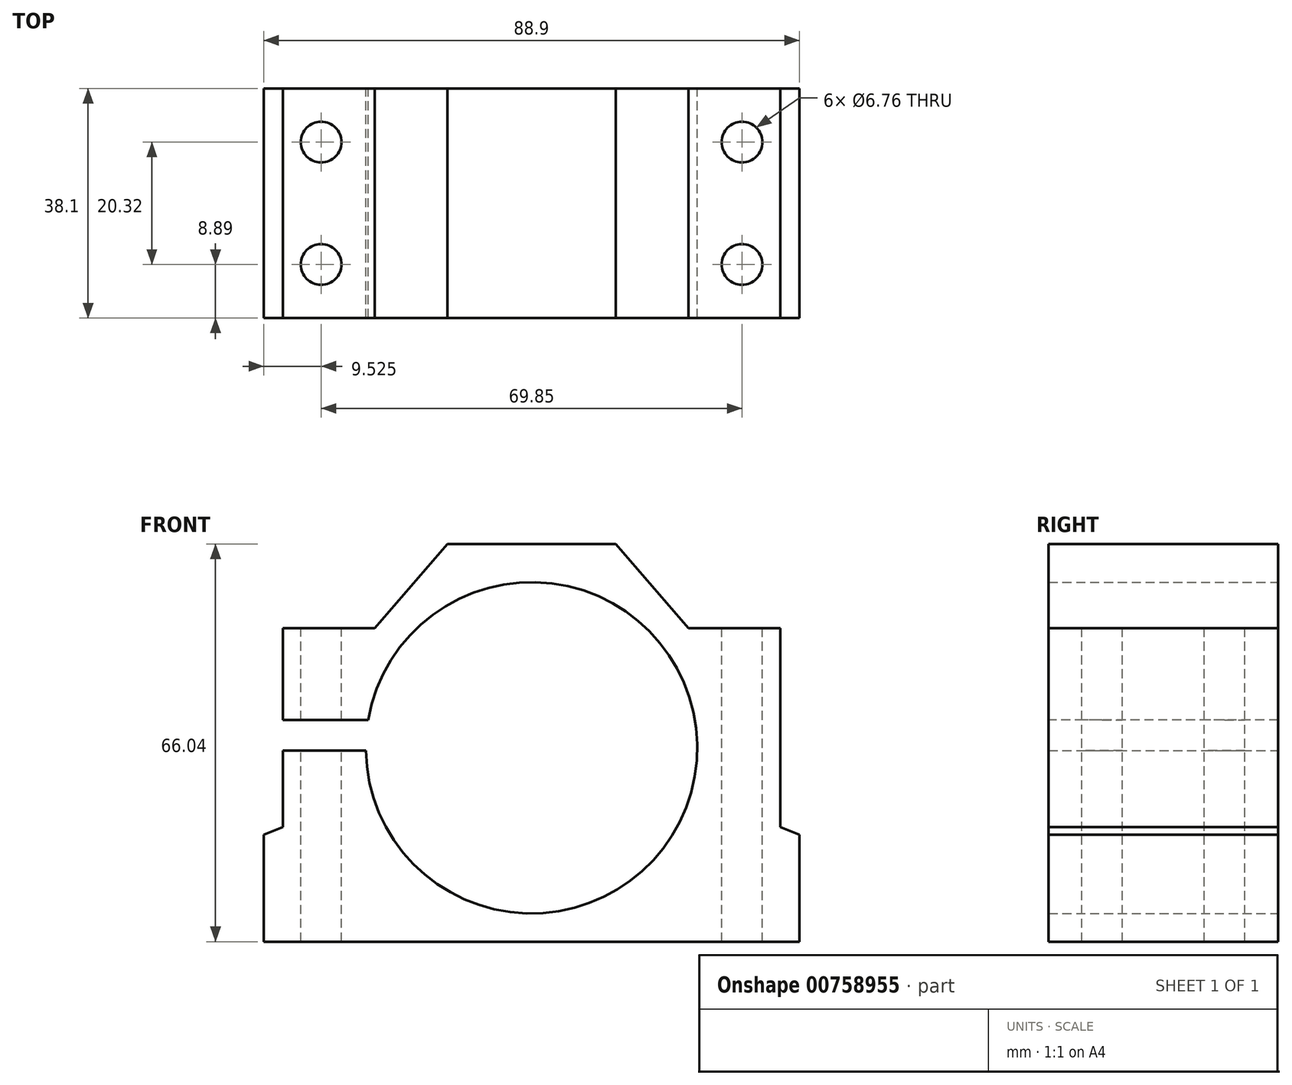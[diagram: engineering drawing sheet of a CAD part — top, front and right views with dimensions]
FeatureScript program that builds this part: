
annotation { "Feature Type Name" : "Feature", "Feature Type Description" : "" }
export const myFeature = defineFeature(function(context is Context, id is Id, definition is map)
    precondition{}
    {
        {
            var Q0;
            Q0=qCreatedBy(makeId("Front.planeOp"),FACE);
            var sketch = newSketch(context, id + "F0", { "sketchPlane" : qUnion([Q0])});
            skLineSegment(sketch, "E0", {"start": v(0, 0) * mm, "end": v(44.45, 0) * mm});
            skLineSegment(sketch, "E1", {"start": v(44.45, 0) * mm, "end": v(44.45, 17.78) * mm});
            skLineSegment(sketch, "E2", {"start": v(44.45, 17.78) * mm, "end": v(41.28, 19.05) * mm});
            skLineSegment(sketch, "E3", {"start": v(41.28, 19.05) * mm, "end": v(41.28, 52.07) * mm});
            skLineSegment(sketch, "E4", {"start": v(41.28, 52.07) * mm, "end": v(26.04, 52.07) * mm});
            skLineSegment(sketch, "E5", {"start": v(26.04, 52.07) * mm, "end": v(13.97, 66.04) * mm});
            skLineSegment(sketch, "E6", {"start": v(13.97, 66.04) * mm, "end": v(0, 66.04) * mm});
            skLineSegment(sketch, "E7.MirrorCS", {"start": v(-41.28, 19.05) * mm, "end": v(-41.28, 52.07) * mm});
            skLineSegment(sketch, "E8.MirrorCS", {"start": v(-44.45, 17.78) * mm, "end": v(-41.28, 19.05) * mm});
            skLineSegment(sketch, "E9.MirrorCS", {"start": v(-41.28, 52.07) * mm, "end": v(-26.04, 52.07) * mm});
            skLineSegment(sketch, "E10.MirrorCS", {"start": v(0, 0) * mm, "end": v(-44.45, 0) * mm});
            skLineSegment(sketch, "E11.MirrorCS", {"start": v(-13.97, 66.04) * mm, "end": v(0, 66.04) * mm});
            skLineSegment(sketch, "E12.MirrorCS", {"start": v(-26.04, 52.07) * mm, "end": v(-13.97, 66.04) * mm});
            skLineSegment(sketch, "E13.MirrorCS", {"start": v(-44.45, 0) * mm, "end": v(-44.45, 17.78) * mm});
            skCircle(sketch, "E14", {"center": v(0, 32.2) * mm, "radius": 27.5 * mm});
            skSolve(sketch);
        }
        {
            var Q0;
            Q0=qSketchRegion(id+"F0",true);
            extrude(context, id + "F1", {"entities" : qUnion([Q0]), "depth" : 38.1 * mm, "offsetDistance" : 25.4 * mm});
        }
        {
            var Q0;
            Q0=makeQuery(id+"F1.opExtrude","CAP_FACE",FACE,{"disambiguationData":[OSD([sQuery(id+"F0.wireOp",EDGE,"E0"),sQuery(id+"F0.wireOp",EDGE,"E1"),sQuery(id+"F0.wireOp",EDGE,"E2"),sQuery(id+"F0.wireOp",EDGE,"E3"),sQuery(id+"F0.wireOp",EDGE,"E4"),sQuery(id+"F0.wireOp",EDGE,"E5"),sQuery(id+"F0.wireOp",EDGE,"E6"),sQuery(id+"F0.wireOp",EDGE,"E7.MirrorCS"),sQuery(id+"F0.wireOp",EDGE,"E8.MirrorCS"),sQuery(id+"F0.wireOp",EDGE,"E9.MirrorCS"),sQuery(id+"F0.wireOp",EDGE,"E10.MirrorCS"),sQuery(id+"F0.wireOp",EDGE,"E11.MirrorCS"),sQuery(id+"F0.wireOp",EDGE,"E12.MirrorCS"),sQuery(id+"F0.wireOp",EDGE,"E13.MirrorCS"),sQuery(id+"F0.wireOp",EDGE,"E14")])],"isStart":false});
            var sketch = newSketch(context, id + "F2", { "sketchPlane" : qUnion([Q0])});
            skLineSegment(sketch, "E15.bottom", {"start": v(-41.28, 31.75) * mm, "end": v(-22.23, 31.75) * mm});
            skLineSegment(sketch, "E15.top", {"start": v(-41.28, 36.83) * mm, "end": v(-22.23, 36.83) * mm});
            skLineSegment(sketch, "E15.left", {"start": v(-41.28, 31.75) * mm, "end": v(-41.28, 36.83) * mm});
            skLineSegment(sketch, "E15.right", {"start": v(-22.23, 31.75) * mm, "end": v(-22.23, 36.83) * mm});
            skSolve(sketch);
        }
        {
            var Q0;
            Q0=qSketchRegion(id+"F2",true);
            extrude(context, id + "F3", {"entities" : qUnion([Q0]), "operationType" : NewBodyOperationType.REMOVE, "endBound" : BoundingType.UP_TO_NEXT, "oppositeDirection" : true, "depth" : 25.4 * mm, "offsetDistance" : 25.4 * mm});
        }
        {
            var Q0;
            Q0=makeQuery(id+"F1.opExtrude","SWEPT_FACE",FACE,{"disambiguationData":[OSD([sQuery(id+"F0.wireOp",EDGE,"E9.MirrorCS")])]});
            var sketch = newSketch(context, id + "F4", { "sketchPlane" : qUnion([Q0])});
            skLineSegment(sketch, "E16", {"start": v(-41.28, -19.05) * mm, "end": v(41.4, -19.05) * mm, "construction": true});
            skPoint(sketch, "E17", {"position": v(-34.93, -29.21) * mm});
            skPoint(sketch, "E18.MirrorP", {"position": v(-34.93, -8.89) * mm});
            skPoint(sketch, "E19.MirrorP", {"position": v(34.93, -8.89) * mm});
            skPoint(sketch, "E20.MirrorP", {"position": v(34.93, -29.21) * mm});
            skSolve(sketch);
        }
        {
            var Q0;
            Q0=sQuery(id+"F4.wireOp",VERTEX,"E18.MirrorP");
            var Q1;
            Q1=sQuery(id+"F4.wireOp",VERTEX,"E17");
            var Q2;
            Q2=sQuery(id+"F4.wireOp",VERTEX,"E19.MirrorP");
            var Q3;
            Q3=sQuery(id+"F4.wireOp",VERTEX,"E20.MirrorP");
            var Q4;
            Q4=makeQuery(id+"F1.opExtrude","SWEPT_BODY",BODY,{"disambiguationData":[OSD([sQuery(id+"F0.wireOp",EDGE,"E0"),sQuery(id+"F0.wireOp",EDGE,"E1"),sQuery(id+"F0.wireOp",EDGE,"E2"),sQuery(id+"F0.wireOp",EDGE,"E3"),sQuery(id+"F0.wireOp",EDGE,"E4"),sQuery(id+"F0.wireOp",EDGE,"E5"),sQuery(id+"F0.wireOp",EDGE,"E6"),sQuery(id+"F0.wireOp",EDGE,"E7.MirrorCS"),sQuery(id+"F0.wireOp",EDGE,"E8.MirrorCS"),sQuery(id+"F0.wireOp",EDGE,"E9.MirrorCS"),sQuery(id+"F0.wireOp",EDGE,"E10.MirrorCS"),sQuery(id+"F0.wireOp",EDGE,"E11.MirrorCS"),sQuery(id+"F0.wireOp",EDGE,"E12.MirrorCS"),sQuery(id+"F0.wireOp",EDGE,"E13.MirrorCS"),sQuery(id+"F0.wireOp",EDGE,"E14")])]});
            hole(context, id + "F5", {"style" : HoleStyle.SIMPLE, "endStyle" : HoleEndStyle.THROUGH, "standardTappedOrClearance" : lookupTablePath({ "standard" : "ANSI", "fit" : "Normal (ASME)", "size" : "1/4", "type" : "Clearance" }), "standardBlindInLast" : lookupTablePath({ "fit" : "Free", "standard" : "ANSI", "size" : "1/4", "type" : "Clearance" }), "holeDiameter" : 6.76 * mm, "majorDiameter" : 6.35 * mm, "isTappedThrough" : true, "tappedDepth" : 12.7 * mm, "tapClearance" : 3, "locations" : qUnion([Q0, Q1, Q2, Q3]), "scope" : qUnion([Q4])});
        }
    });
